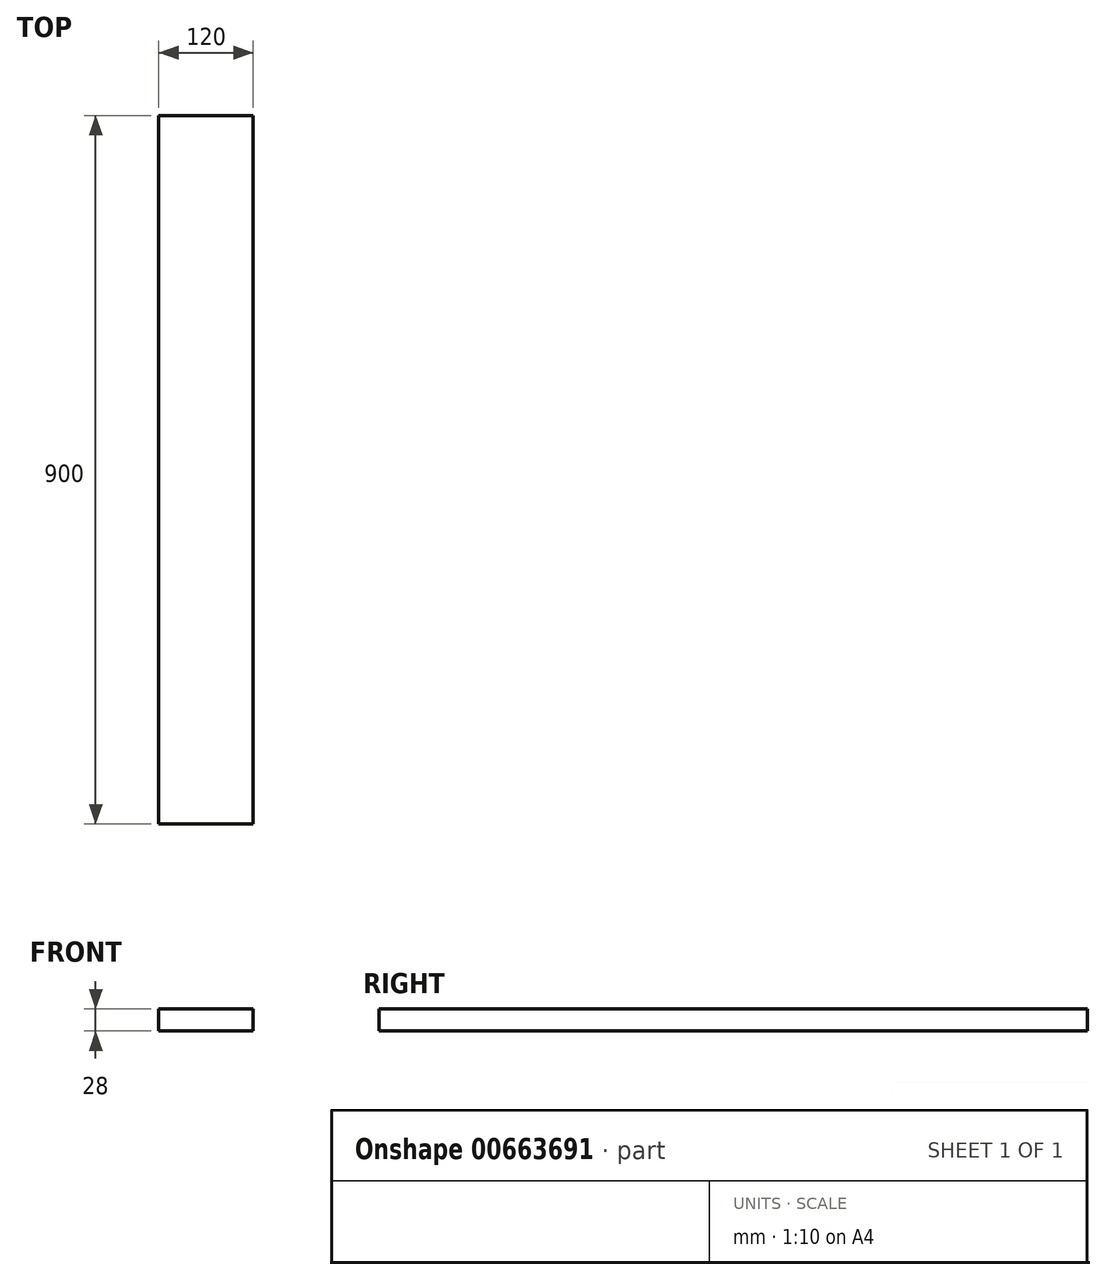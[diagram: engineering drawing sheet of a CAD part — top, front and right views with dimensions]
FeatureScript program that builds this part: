
annotation { "Feature Type Name" : "Feature", "Feature Type Description" : "" }
export const myFeature = defineFeature(function(context is Context, id is Id, definition is map)
    precondition{}
    {
        {
            var Q0;
            Q0=qCreatedBy(makeId("Front.planeOp"),FACE);
            var sketch = newSketch(context, id + "F0", { "sketchPlane" : qUnion([Q0])});
            skLineSegment(sketch, "E0.bottom", {"start": v(0, 112.73) * mm, "end": v(120, 112.73) * mm});
            skLineSegment(sketch, "E0.top", {"start": v(0, 140.73) * mm, "end": v(120, 140.73) * mm});
            skLineSegment(sketch, "E0.left", {"start": v(0, 112.73) * mm, "end": v(0, 140.73) * mm});
            skLineSegment(sketch, "E0.right", {"start": v(120, 112.73) * mm, "end": v(120, 140.73) * mm});
            skSolve(sketch);
        }
        {
            var Q0;
            Q0 = qSketchRegion(id + "F0", true);
            extrude(context, id + "F1", {"entities" : qUnion([Q0]), "depth" : 900 * mm, "offsetDistance" : 25 * mm});
        }
    });
